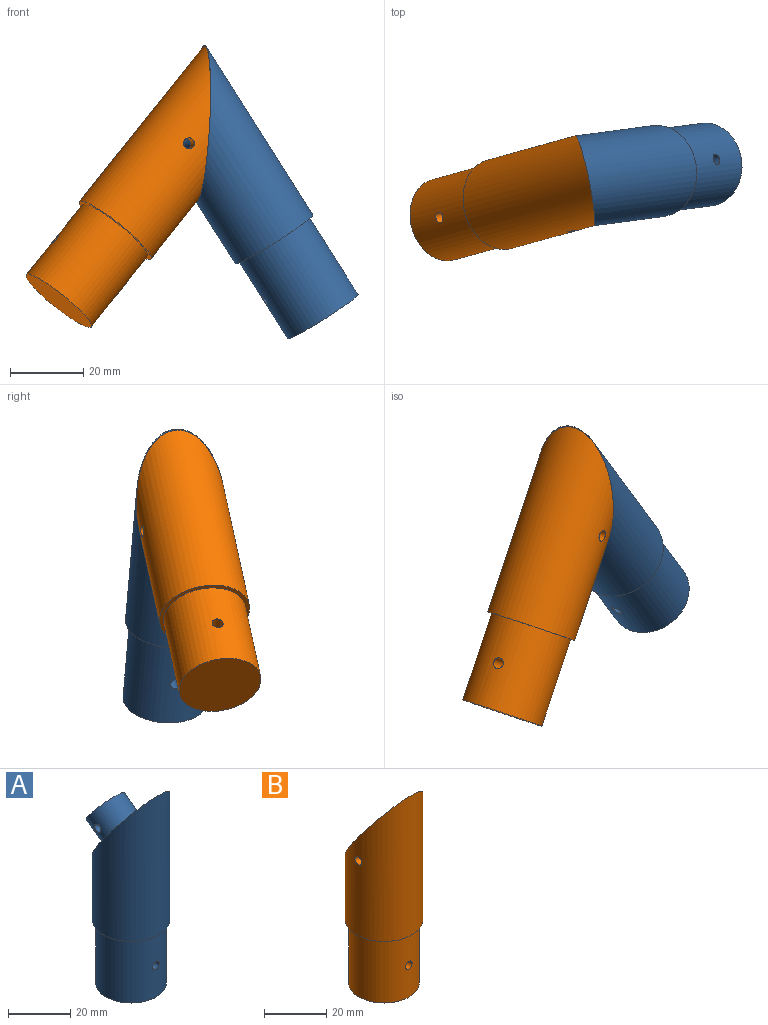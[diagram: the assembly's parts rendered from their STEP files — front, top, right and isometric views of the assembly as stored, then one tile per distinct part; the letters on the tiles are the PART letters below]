
ASSEMBLY  parts=2 mates=1
PART A: 9 faces, bbox 25x28.7x80.2 mm
  f0: cylinder r=7.5mm len=18.01mm, axis (0,-0.81,-0.59), area 457mm2, adj f5,f6,f7
  f1: cylinder r=12.5mm len=55.24mm, axis (0,0,-1), area 2968.4mm2, adj f4,f5
  f2: cylinder r=11.35mm len=25mm, axis (0,0,-1), area 1768.6mm2, adj f3,f4,f8
  f3: plane 22.7x22.7mm, normal (0,0,-1), area 404.7mm2, adj f2
  f4: plane 25x25mm, normal (0,0,-1), area 86.2mm2, adj f1,f2
  f5: plane 34.41x25mm, normal (0,0.81,0.59), area 658.4mm2, adj f0,f1
  f6: plane 15x12.14mm, normal (0,0.81,0.59), area 176.7mm2, adj f0
  f7: cylinder r=1.5mm len=15mm, axis (1,0,0), area 139.9mm2, adj f0
  f8: cylinder r=1.5mm len=22.7mm, axis (0,-1,0), area 213mm2, adj f2
PART B: 10 faces, bbox 25x25x80.2 mm
  f0: cylinder r=12.5mm len=55.24mm, axis (0,0,-1), area 2954.2mm2, adj f4,f5,f8,f9
  f1: cylinder r=8mm len=18.82mm, axis (0,0.81,0.59), area 488.5mm2, adj f5,f6,f8,f9
  f2: cylinder r=11.35mm len=25mm, axis (0,0,-1), area 1768.6mm2, adj f3,f4,f7
  f3: plane 22.7x22.7mm, normal (0,0,-1), area 404.7mm2, adj f2
  f4: plane 25x25mm, normal (0,0,-1), area 86.2mm2, adj f0,f2
  f5: plane 34.41x25mm, normal (0,0.81,0.59), area 634.1mm2, adj f0,f1
  f6: plane 16x12.94mm, normal (0,0.81,0.59), area 201.1mm2, adj f1
  f7: cylinder r=1.5mm len=22.7mm, axis (0,-1,0), area 213mm2, adj f2
  f8: cylinder r=1.5mm len=4.64mm, axis (1,0,0), area 42.4mm2, adj f0,f1
  f9: cylinder r=1.5mm len=4.64mm, axis (1,0,0), area 42.4mm2, adj f0,f1
PLACE A rot(axis=(-0.24,-0.25,0.94),106.4deg) t=(-50.04,-18.17,7.1)mm
PLACE B rot(axis=(-0.4,0.28,-0.87),86.9deg) t=(-122.16,-33.31,11.39)mm
MATE fastened B.f5 <-> A.f5  axis (0.98,0.2,-0.06) through (-83.42,-22.62,61.72)mm
